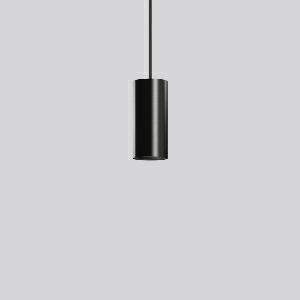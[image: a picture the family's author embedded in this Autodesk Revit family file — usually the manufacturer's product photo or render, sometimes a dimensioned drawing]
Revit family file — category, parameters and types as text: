
# Revit family: deecos_p_mini_911523_003_76_3659
name_source: partatom
category: Lighting Fixtures
units: mm (PartAtom-declared; Revit-internal decimal feet)

## family parameters
Cut with Voids When Loaded = No
Host = Face
Light Source = No
Part Type = Normal
Room Calculation Point = No
Round Connector Dimension = Use Diameter
Shared = No

## types (1)
- DEECOS P mini (1 x LED Modul 930, 3650 lm, 3000)
    Apparent Load = 29 VA
    Approval mark = CE
    CIE Flux Codes = 95 99 100 100 100
    Color Rendering = 90
    Color Temperature = 3000
    Default Elevation = 1800 mm
    Description = Series: DEECOS P mini
Cylindrical pendant luminaire. Housing: die-cast aluminium, powder-coated. Canopy made of powder-coated sheet steel with magnetic attachment. Optical assembly with reflector made of MIRO-Silver with 98% total light reflection for outstanding efficiency - can be changed without tools. Best colour rendering index Ra>90. Transparent pendant cable 5 m, can be shortened, with integrated steel cable. High quality converter without flickering and stroboscopic effect. The following accessories can be mounted without use of tools: interchangeable lenses, honeycomb louvre, clear and frosted diffusers, white interchangeable plastic ring. Decorative recessed suspension set available as accessory.Suitable for accessory Deecos P Tube cylinder extensions 0.5 m, 0.75 m or 1 m. 
Colour: deep black, matt (RAL 9005)
Diameter: 87 mm
Height: 195 mm
Suspension length: 5000 mm
Lamp: LED
Socket: without socket
Colour temperature: 3000K
Colour rendering index (CRI): 92
System power: 29 W
Rated luminous flux: 3650 lm
Luminous efficiency: 126 lm/W
Control gear: Converter, dimmable, DALI
Protection class: I
Type of protection: IP 20
    Height = 195 mm
    Lamp = 1 x LED Modul 930
    Lamp Light Flux = 3650 lm
    Lamp count = 1
    Length = 87 mm
    Lifetime = 50000 h
    Luminous efficacy = 126 lm/W
    Manufacturer = RZB
    ModVariant = No
    Model = 911523.003.76
    Mounting Place = Ceiling
    Mounting Type = Pendant
    Number of Poles = 1
    OnlyDefault = Yes
    Power Factor = 1
    Product Name = DEECOS P mini
    Product group = Pendant luminaires
    ProductGroupID = 902
    Protection Class = Protection class I
    Protection Degree = IP 20
    RLX_Detail_Level = 1
    RLX_Emergency_Light_Flux = 0 lm
    RLX_Emergency_Type = 0
    RLX_Emergency_Type_DB = No
    RlxData = <blob elided: 56465 chars, md5=0530a992>
    Socket = socket
    Standby Power = 0 W
    System Light Flux = 3650 lm
    System Power = 29 W
    Type Comments = Product without accessories
    Type Image = 911476.003.jpg
    URL = http://relux.com
    VarID = ---
    Voltage = 230 V
    Voltage Range = 220-240 V
    Weight = 0.00 kg
    Width = 0 mm  [stored 0 ft]

note: [stored X ft] marks values corroborated as IEEE doubles in the binary element streams (Revit-internal decimal feet)

## geometry (parser evidence)
native form markers: Blend x4, Sweep x13
no freeform markers — native parametric forms only
